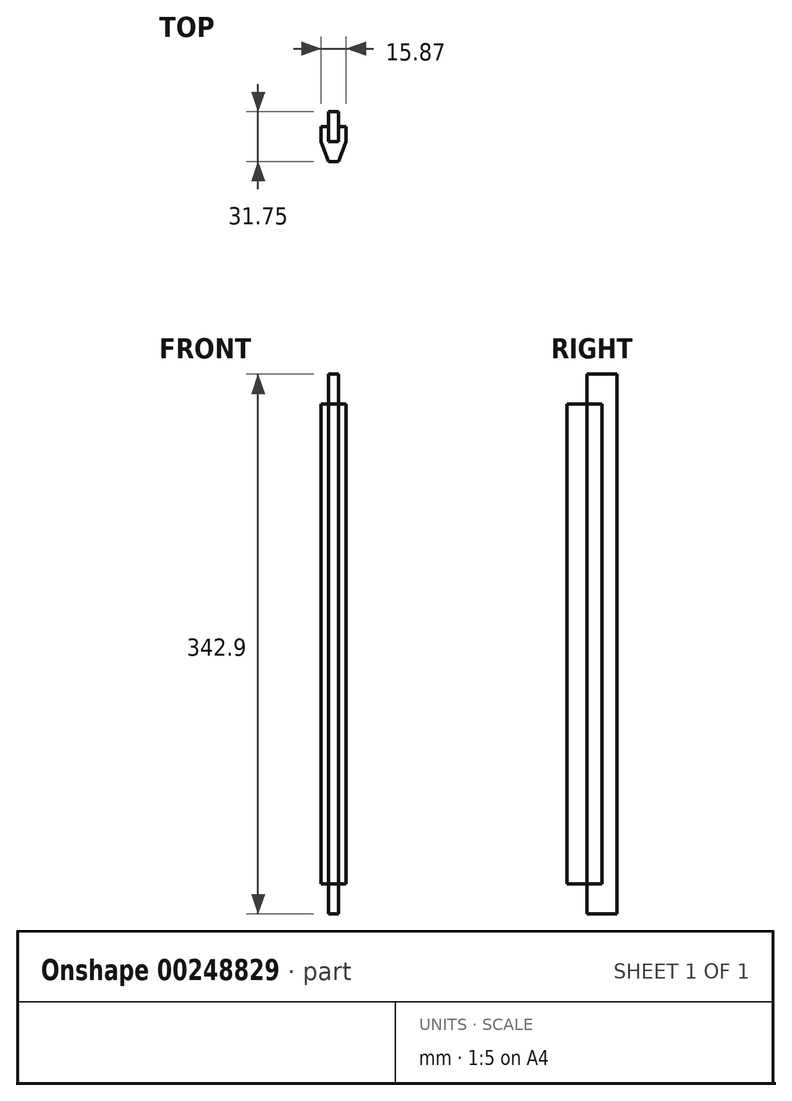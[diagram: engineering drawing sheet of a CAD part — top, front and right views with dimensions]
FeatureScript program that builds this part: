
annotation { "Feature Type Name" : "Feature", "Feature Type Description" : "" }
export const myFeature = defineFeature(function(context is Context, id is Id, definition is map)
    precondition{}
    {
        {
            var Q0;
            Q0=qCreatedBy(makeId("Top.planeOp"),FACE);
            var sketch = newSketch(context, id + "F0", { "sketchPlane" : qUnion([Q0])});
            skLineSegment(sketch, "E0", {"start": v(0, 0) * mm, "end": v(0, -9.52) * mm});
            skLineSegment(sketch, "E1", {"start": v(0, -9.52) * mm, "end": v(-4.76, -9.52) * mm});
            skLineSegment(sketch, "E2", {"start": v(-4.76, -19.05) * mm, "end": v(0, -31.75) * mm});
            skLineSegment(sketch, "E3", {"start": v(0, -31.75) * mm, "end": v(6.35, -31.75) * mm});
            skLineSegment(sketch, "E4", {"start": v(6.35, -31.75) * mm, "end": v(11.11, -19.05) * mm});
            skLineSegment(sketch, "E5", {"start": v(6.35, -9.52) * mm, "end": v(11.11, -9.52) * mm});
            skLineSegment(sketch, "E6", {"start": v(6.35, -9.52) * mm, "end": v(6.35, 0) * mm});
            skLineSegment(sketch, "E7", {"start": v(-4.76, -9.52) * mm, "end": v(-4.76, -19.05) * mm});
            skLineSegment(sketch, "E8", {"start": v(11.11, -19.05) * mm, "end": v(11.11, -9.52) * mm});
            skLineSegment(sketch, "E9", {"start": v(0, 0) * mm, "end": v(6.35, 0) * mm});
            skSolve(sketch);
        }
        {
            var Q0;
            Q0=makeQuery(id+"F0.imprint","IMPRINT",FACE,{"disambiguationData":[TD([[makeQuery(id+"F0.imprint","IMPRINT",EDGE,{"derivedFrom":sQuery(id+"F0.wireOp",EDGE,"E0")}),1.0]])]});
            extrude(context, id + "F1", {"entities" : qUnion([Q0]), "depth" : 304.8 * mm});
        }
        {
            var Q0;
            Q0=makeQuery(id+"F1.opExtrude","CAP_FACE",FACE,{"disambiguationData":[OSD([sQuery(id+"F0.wireOp",EDGE,"E0"),sQuery(id+"F0.wireOp",EDGE,"E1"),sQuery(id+"F0.wireOp",EDGE,"E2"),sQuery(id+"F0.wireOp",EDGE,"E3"),sQuery(id+"F0.wireOp",EDGE,"E4"),sQuery(id+"F0.wireOp",EDGE,"E5"),sQuery(id+"F0.wireOp",EDGE,"E6"),sQuery(id+"F0.wireOp",EDGE,"E7"),sQuery(id+"F0.wireOp",EDGE,"E8"),sQuery(id+"F0.wireOp",EDGE,"E9")])],"isStart":true});
            var sketch = newSketch(context, id + "F2", { "sketchPlane" : qUnion([Q0])});
            skLineSegment(sketch, "E10", {"start": v(6.35, 19.05) * mm, "end": v(6.35, 9.52) * mm});
            skLineSegment(sketch, "E11", {"start": v(6.35, 19.05) * mm, "end": v(0, 19.05) * mm});
            skLineSegment(sketch, "E12", {"start": v(0, 19.05) * mm, "end": v(0, 9.52) * mm});
            skSolve(sketch);
        }
        {
            var Q0;
            Q0=makeQuery(id+"F2.imprint","IMPRINT",FACE,{"disambiguationData":[TD([[makeQuery(id+"F2.imprint","IMPRINT",EDGE,{"derivedFrom":sQuery(id+"F2.wireOp",EDGE,"E10")}),-1.0]])]});
            extrude(context, id + "F3", {"entities" : qUnion([Q0]), "operationType" : NewBodyOperationType.ADD, "depth" : 19.05 * mm});
        }
        {
            var Q0;
            Q0=makeQuery(id+"F1.opExtrude","CAP_FACE",FACE,{"disambiguationData":[OSD([sQuery(id+"F0.wireOp",EDGE,"E0"),sQuery(id+"F0.wireOp",EDGE,"E1"),sQuery(id+"F0.wireOp",EDGE,"E2"),sQuery(id+"F0.wireOp",EDGE,"E3"),sQuery(id+"F0.wireOp",EDGE,"E4"),sQuery(id+"F0.wireOp",EDGE,"E5"),sQuery(id+"F0.wireOp",EDGE,"E6"),sQuery(id+"F0.wireOp",EDGE,"E7"),sQuery(id+"F0.wireOp",EDGE,"E8"),sQuery(id+"F0.wireOp",EDGE,"E9")])],"isStart":false});
            var sketch = newSketch(context, id + "F4", { "sketchPlane" : qUnion([Q0])});
            skLineSegment(sketch, "E13", {"start": v(0, -9.52) * mm, "end": v(0, -19.05) * mm});
            skLineSegment(sketch, "E14", {"start": v(0, -19.05) * mm, "end": v(6.35, -19.05) * mm});
            skLineSegment(sketch, "E15", {"start": v(6.35, -19.05) * mm, "end": v(6.35, -9.52) * mm});
            skSolve(sketch);
        }
        {
            var Q0;
            Q0=makeQuery(id+"F4.imprint","IMPRINT",FACE,{"disambiguationData":[TD([[makeQuery(id+"F4.imprint","IMPRINT",EDGE,{"derivedFrom":sQuery(id+"F4.wireOp",EDGE,"E13")}),1.0]])]});
            extrude(context, id + "F5", {"entities" : qUnion([Q0]), "operationType" : NewBodyOperationType.ADD, "depth" : 19.05 * mm});
        }
    });
